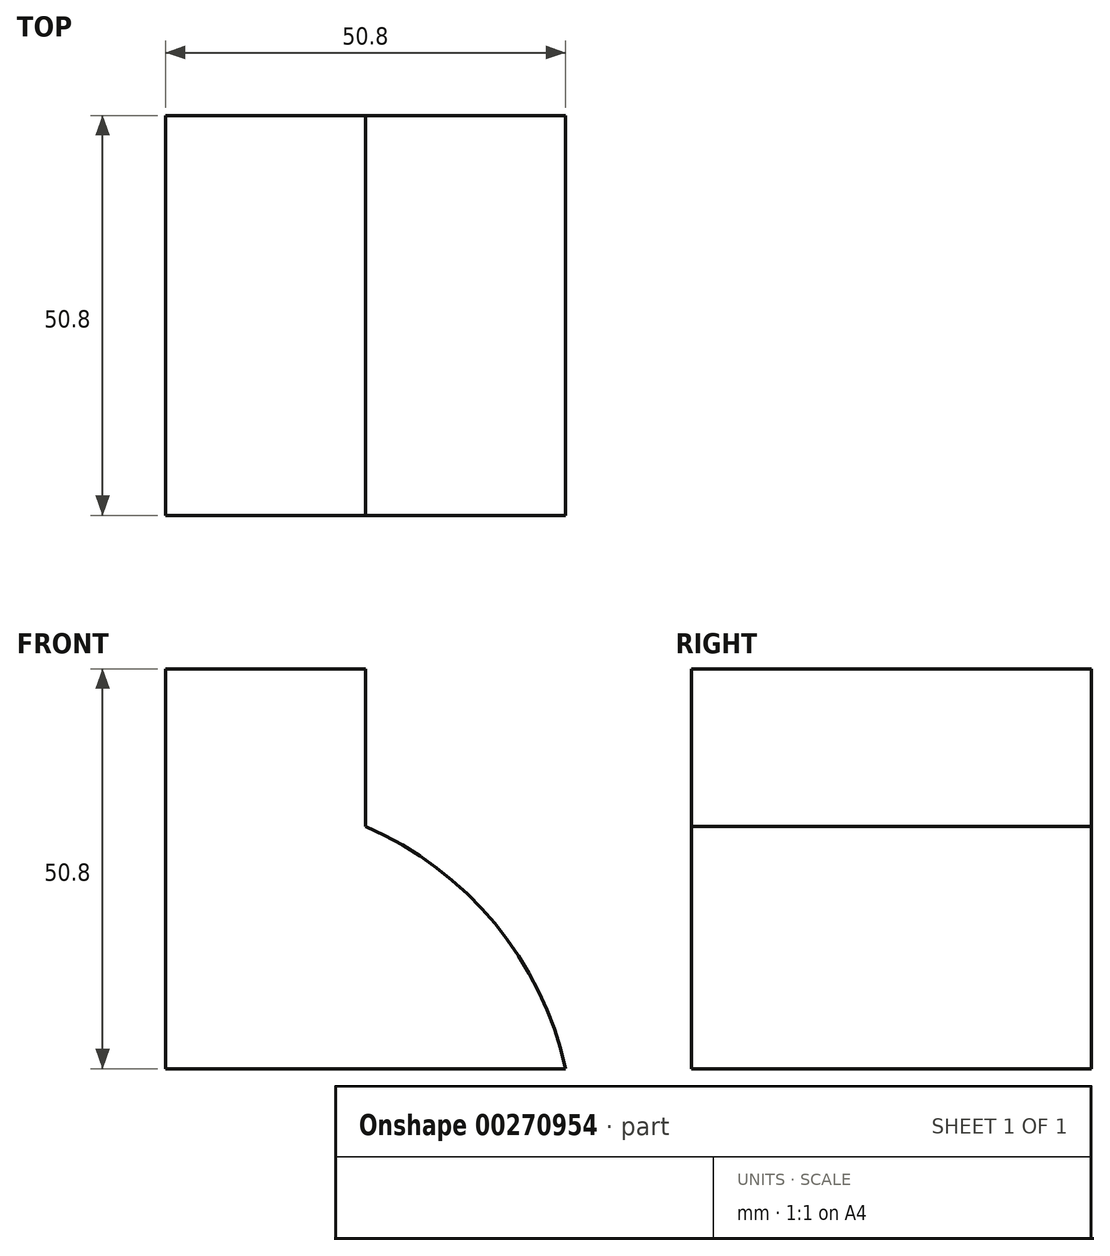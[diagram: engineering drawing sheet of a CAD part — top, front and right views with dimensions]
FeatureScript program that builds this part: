
annotation { "Feature Type Name" : "Feature", "Feature Type Description" : "" }
export const myFeature = defineFeature(function(context is Context, id is Id, definition is map)
    precondition{}
    {
        {
            var Q0;
            Q0=qCreatedBy(makeId("Front.planeOp"),FACE);
            var sketch = newSketch(context, id + "F0", { "sketchPlane" : qUnion([Q0])});
            skLineSegment(sketch, "E0", {"start": v(-65.69, 0) * mm, "end": v(-65.69, 50.8) * mm});
            skLineSegment(sketch, "E1", {"start": v(-65.69, 50.8) * mm, "end": v(-40.29, 50.8) * mm});
            skLineSegment(sketch, "E2", {"start": v(-40.29, 50.8) * mm, "end": v(-40.29, 30.74) * mm});
            skLineSegment(sketch, "E3", {"start": v(-65.69, 0) * mm, "end": v(-14.89, 0) * mm});
            skArc(sketch, "E4", {"start": v(-14.89, 0) * mm, "mid": v(-23.87, 18.44) * mm, "end": v(-40.29, 30.74) * mm});
            skSolve(sketch);
        }
        {
            var Q0;
            Q0 = qSketchRegion(id + "F0", true);
            extrude(context, id + "F1", {"entities" : qUnion([Q0]), "depth" : 50.8 * mm});
        }
    });
